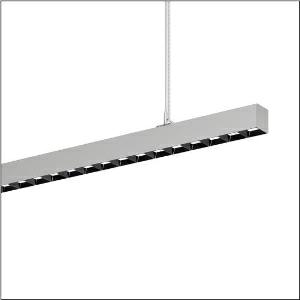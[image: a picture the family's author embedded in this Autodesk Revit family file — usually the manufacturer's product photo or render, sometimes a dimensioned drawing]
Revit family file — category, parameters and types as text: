
# Revit family: silica_r__21_51mx32tctds_853f
name_source: partatom
category: Lighting Fixtures
units: mm (PartAtom-declared; Revit-internal decimal feet)

## family parameters
Cut with Voids When Loaded = No
Host = Face
Light Source = No
Part Type = Normal
Room Calculation Point = No
Round Connector Dimension = Use Diameter
Shared = No

## types (1)
- --- (1 x LED, 15540 lm, 133.6 W, 6500K)
    Apparent Load = 134 VA
    CIE Flux Codes = 84 99 100 60 100
    Color Rendering = 80
    Color Temperature = 6500K
    Default Elevation = 1800 mm
    Description = Silica® 21, office luminaire, primary light control with darklight reflector, of PMMA, black, CAT 2 (L<= 3000cd/m²), light emission: direct/indirect distribution, primary light characteristic: symmetric, installation type: suspended mounting, LED, rated luminous flux: 15.540lm, luminous efficacy: 111lm/W, light colour: 8tw, colour temperature: 2700..6500K, control gear: ECG DALI, with terminal, 3+2-pole, max. 2.5mm², mains connection: 220..240V, AC, 50/60Hz, rated input power: 140.3W, luminaire housing, of aluminium, metallic grey (RAL 9006), length: 3.004mm, width: 53mm, height: 53mm, protection rating (complete): IP20, insulation class (complete): insulation class I (protective earthing), certification: CE, permissible operating ambient temperature: 0..+35°C, standard: EN 50419, packaging unit: 1 piece
    Height = 53 mm
    Lamp = 1 x LED
    Lamp Light Flux = 15540 lm
    Lamp Power = 133.6 W
    Lamp count = 1
    Length = 3004 mm
    Luminous efficacy = 116 lm/W
    Manufacturer = Siteco
    ModVariant = No
    Model = 51MX32TCTDS
    Mounting Place = Ceiling
    Mounting Type = Pendant
    Number of Poles = 1
    OnlyDefault = Yes
    Power Factor = 1
    Product Name = Silica® 21
    Product group = office luminaire | ceiling pendant
    ProductGroupID = 902
    Protection Class = Protection class I
    Protection Degree = IP 20
    RLX_Detail_Level = 1
    RLX_Emergency_Light_Flux = 0 lm
    RLX_Emergency_Type = 0
    RLX_Emergency_Type_DB = No
    RlxData = <blob elided: 61677 chars, md5=9a3a8d8f>
    Socket = socket
    Standby Power = 0 W
    System Light Flux = 15540 lm
    System Power = 134 W
    Type Comments = individual setting
    Type Image = l_1297751.jpg
    URL = http://relux.com
    VarID = @adj_071239
    Voltage = 0 V
    Weight = 0.00 kg
    Width = 53 mm

## geometry (parser evidence)
native form markers: Blend x4, Sweep x14
no freeform markers — native parametric forms only
